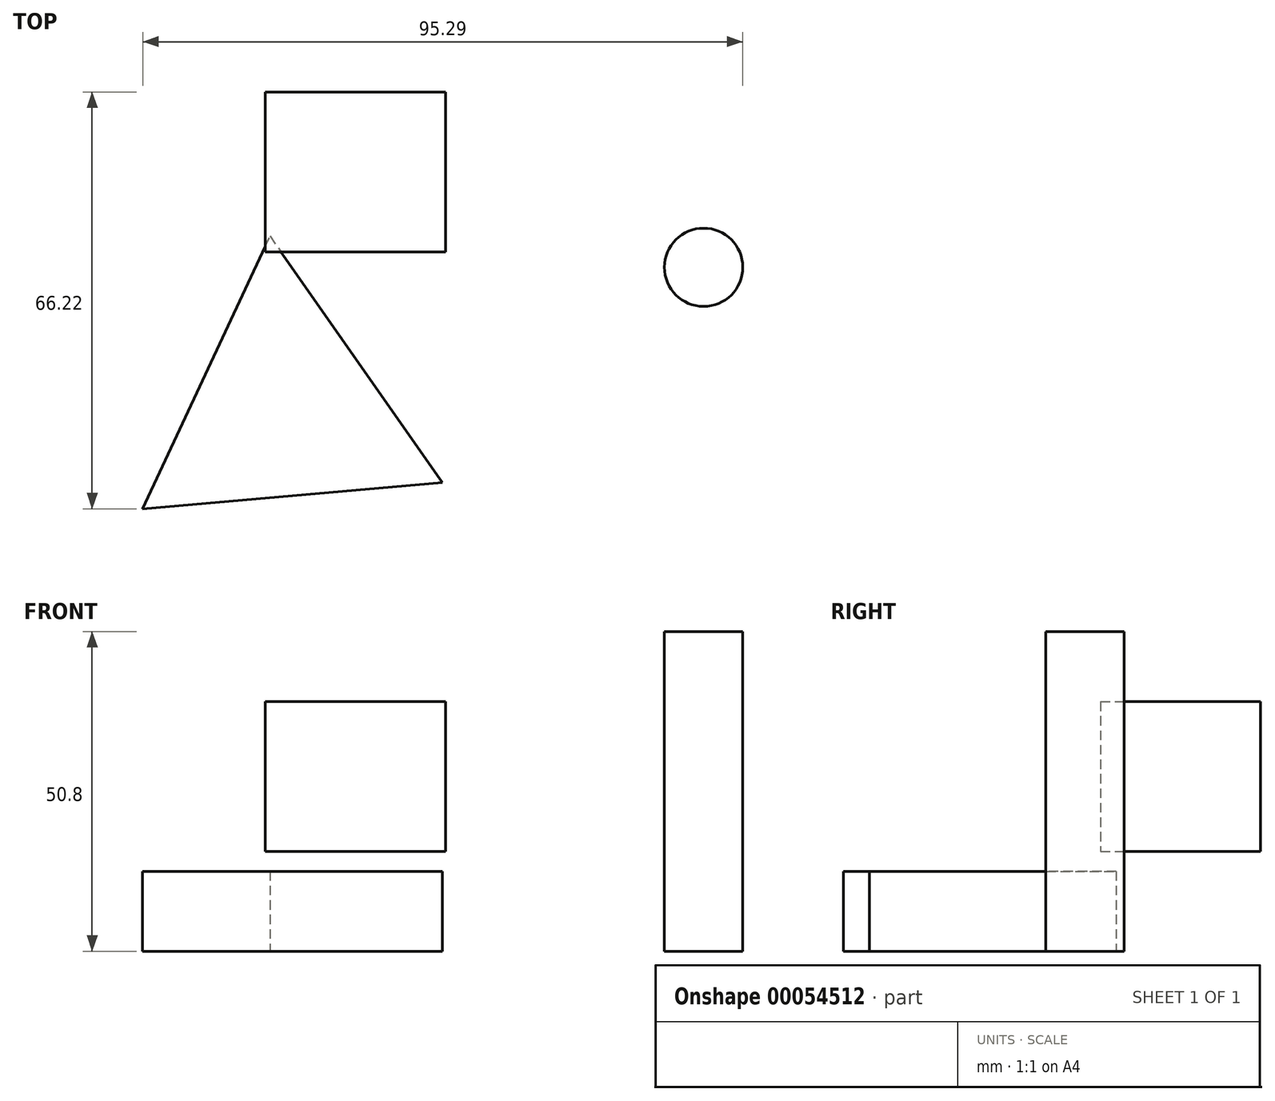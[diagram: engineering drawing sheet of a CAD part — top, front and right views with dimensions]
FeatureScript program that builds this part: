
annotation { "Feature Type Name" : "Feature", "Feature Type Description" : "" }
export const myFeature = defineFeature(function(context is Context, id is Id, definition is map)
    precondition{}
    {
        {
            var Q0;
            Q0=qCreatedBy(makeId("Front.planeOp"),FACE);
            var sketch = newSketch(context, id + "F0", { "sketchPlane" : qUnion([Q0])});
            skLineSegment(sketch, "E0.bottom", {"start": v(-51.15, 39.65) * mm, "end": v(-22.5, 39.65) * mm});
            skLineSegment(sketch, "E0.top", {"start": v(-51.15, 15.84) * mm, "end": v(-22.5, 15.84) * mm});
            skLineSegment(sketch, "E0.left", {"start": v(-51.15, 39.65) * mm, "end": v(-51.15, 15.84) * mm});
            skLineSegment(sketch, "E0.right", {"start": v(-22.5, 39.65) * mm, "end": v(-22.5, 15.84) * mm});
            skSolve(sketch);
        }
        {
            var Q0;
            Q0=qCreatedBy(makeId("Top.planeOp"),FACE);
            var sketch = newSketch(context, id + "F1", { "sketchPlane" : qUnion([Q0])});
            skCircle(sketch, "E1", {"center": v(18.46, -27.86) * mm, "radius": 6.22 * mm});
            skSolve(sketch);
        }
        {
            var Q0;
            Q0=makeQuery(id+"F1.imprint","IMPRINT",FACE,{"disambiguationData":[TD([[makeQuery(id+"F1.imprint","IMPRINT",EDGE,{"derivedFrom":sQuery(id+"F1.wireOp",EDGE,"E1")}),1.0]])]});
            extrude(context, id + "F2", {"entities" : qUnion([Q0]), "depth" : 50.8 * mm});
        }
        {
            var Q0;
            Q0=makeQuery(id+"F0.imprint","IMPRINT",FACE,{"disambiguationData":[TD([[makeQuery(id+"F0.imprint","IMPRINT",EDGE,{"derivedFrom":sQuery(id+"F0.wireOp",EDGE,"E0.bottom")}),-1.0]])]});
            extrude(context, id + "F3", {"entities" : qUnion([Q0]), "depth" : 25.4 * mm});
        }
        {
            var Q0;
            Q0=qCreatedBy(makeId("Top.planeOp"),FACE);
            var sketch = newSketch(context, id + "F4", { "sketchPlane" : qUnion([Q0])});
            skCircle(sketch, "E2.cCircle", {"center": v(-48.01, -50.4) * mm, "radius": 13.8 * mm, "construction": true});
            skLineSegment(sketch, "E2.0", {"start": v(-50.4, -22.9) * mm, "end": v(-23, -62.08) * mm});
            skLineSegment(sketch, "E2.1", {"start": v(-23, -62.08) * mm, "end": v(-70.62, -66.22) * mm});
            skLineSegment(sketch, "E2.2", {"start": v(-70.62, -66.22) * mm, "end": v(-50.4, -22.9) * mm});
            skPoint(sketch, "E2.0.midPoint", {"position": v(-36.7, -42.5) * mm});
            skSolve(sketch);
        }
        {
            var Q0;
            Q0=makeQuery(id+"F4.imprint","IMPRINT",FACE,{"disambiguationData":[TD([[makeQuery(id+"F4.imprint","IMPRINT",EDGE,{"derivedFrom":sQuery(id+"F4.wireOp",EDGE,"E2.0")}),-1.0]])]});
            extrude(context, id + "F5", {"entities" : qUnion([Q0]), "operationType" : NewBodyOperationType.ADD, "depth" : 12.7 * mm});
        }
    });
